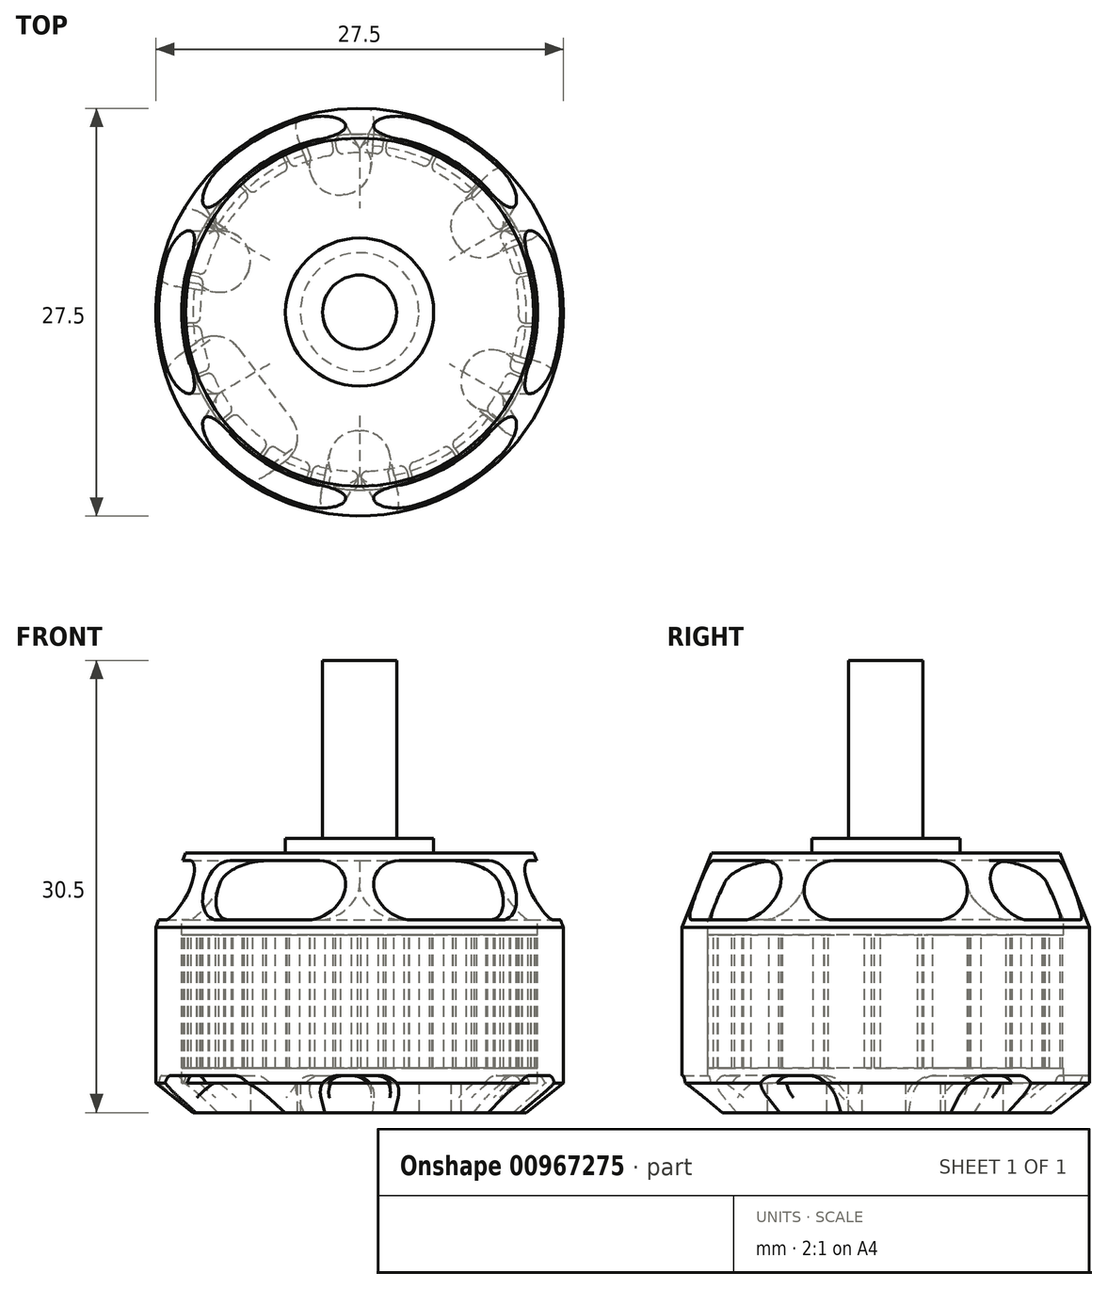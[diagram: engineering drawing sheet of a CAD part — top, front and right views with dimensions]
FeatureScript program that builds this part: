
annotation { "Feature Type Name" : "Feature", "Feature Type Description" : "" }
export const myFeature = defineFeature(function(context is Context, id is Id, definition is map)
    precondition{}
    {
        {
            var Q0;
            Q0=qCreatedBy(makeId("Top.planeOp"),FACE);
            var sketch = newSketch(context, id + "F0", { "sketchPlane" : qUnion([Q0])});
            skCircle(sketch, "E0", {"center": v(0, 0) * mm, "radius": 13.75 * mm});
            skSolve(sketch);
        }
        {
            var Q0;
            Q0=makeQuery(id+"F0.imprint","IMPRINT",FACE,{"disambiguationData":[TD([[makeQuery(id+"F0.imprint","IMPRINT",EDGE,{"derivedFrom":sQuery(id+"F0.wireOp",EDGE,"E0")}),1.0]])]});
            extrude(context, id + "F1", {"entities" : qUnion([Q0]), "depth" : 17.5 * mm});
        }
        {
            var Q0;
            Q0=makeQuery(id+"F1.opExtrude","CAP_FACE",FACE,{"disambiguationData":[OSD([sQuery(id+"F0.wireOp",EDGE,"E0")])],"isStart":false});
            var sketch = newSketch(context, id + "F2", { "sketchPlane" : qUnion([Q0])});
            skCircle(sketch, "E1", {"center": v(0, 0) * mm, "radius": 5 * mm});
            skSolve(sketch);
        }
        {
            var Q0;
            Q0=makeQuery(id+"F2.imprint","IMPRINT",FACE,{"disambiguationData":[TD([[makeQuery(id+"F2.imprint","IMPRINT",EDGE,{"derivedFrom":sQuery(id+"F2.wireOp",EDGE,"E1")}),1.0]])]});
            extrude(context, id + "F3", {"entities" : qUnion([Q0]), "operationType" : NewBodyOperationType.ADD, "depth" : 1 * mm});
        }
        {
            var Q0;
            Q0=makeQuery(id+"F3.opExtrude","CAP_FACE",FACE,{"disambiguationData":[OSD([sQuery(id+"F2.wireOp",EDGE,"E1")])],"isStart":false});
            var sketch = newSketch(context, id + "F4", { "sketchPlane" : qUnion([Q0])});
            skCircle(sketch, "E2", {"center": v(0, 0) * mm, "radius": 2.5 * mm});
            skSolve(sketch);
        }
        {
            var Q0;
            Q0=makeQuery(id+"F4.imprint","IMPRINT",FACE,{"disambiguationData":[TD([[makeQuery(id+"F4.imprint","IMPRINT",EDGE,{"derivedFrom":sQuery(id+"F4.wireOp",EDGE,"E2")}),1.0]])]});
            extrude(context, id + "F5", {"entities" : qUnion([Q0]), "operationType" : NewBodyOperationType.ADD, "depth" : 12 * mm});
        }
        {
            var Q0;
            Q0=makeQuery(id+"F1.opExtrude","CAP_EDGE",EDGE,{"disambiguationData":[OSD([sQuery(id+"F0.wireOp",EDGE,"E0")])],"isStart":false});
            chamfer(context, id + "F6", {"entities" : qUnion([Q0]), "chamferType" : ChamferType.TWO_OFFSETS, "width1" : 2 * mm, "oppositeDirection" : false, "width2" : 5 * mm, "tangentPropagation" : true});
        }
        {
            var Q0;
            Q0=makeQuery(id+"F1.opExtrude","CAP_EDGE",EDGE,{"disambiguationData":[OSD([sQuery(id+"F0.wireOp",EDGE,"E0")])],"isStart":true});
            chamfer(context, id + "F7", {"entities" : qUnion([Q0]), "chamferType" : ChamferType.TWO_OFFSETS, "width1" : 2 * mm, "oppositeDirection" : false, "width2" : 2.5 * mm, "tangentPropagation" : true});
        }
        {
            var Q0;
            Q0=qCreatedBy(makeId("Right.planeOp"),FACE);
            var sketch = newSketch(context, id + "F8", { "sketchPlane" : qUnion([Q0])});
            skLineSegment(sketch, "E3.bottom", {"start": v(-3.5, 17) * mm, "end": v(3.5, 17) * mm});
            skLineSegment(sketch, "E3.top", {"start": v(-3.5, 13) * mm, "end": v(3.5, 13) * mm});
            skLineSegment(sketch, "E3.left", {"start": v(-3.5, 17) * mm, "end": v(-3.5, 13) * mm, "construction": true});
            skLineSegment(sketch, "E3.right", {"start": v(3.5, 17) * mm, "end": v(3.5, 13) * mm, "construction": true});
            skArc(sketch, "E4", {"start": v(-3.5, 17) * mm, "mid": v(-5.5, 15) * mm, "end": v(-3.5, 13) * mm});
            skArc(sketch, "E5", {"start": v(3.5, 13) * mm, "mid": v(5.5, 15) * mm, "end": v(3.5, 17) * mm});
            skSolve(sketch);
        }
        {
            var Q0;
            Q0=qSketchRegion(id+"F8",true);
            extrude(context, id + "F9", {"entities" : qUnion([Q0]), "endBound" : BoundingType.SYMMETRIC, "oppositeDirection" : true, "depth" : 30 * mm});
        }
        {
            var Q0;
            Q0=makeQuery(id+"F9.opExtrude","SWEPT_BODY",BODY,{"disambiguationData":[OSD([sQuery(id+"F8.wireOp",EDGE,"E3.bottom"),sQuery(id+"F8.wireOp",EDGE,"E3.top"),sQuery(id+"F8.wireOp",EDGE,"E4"),sQuery(id+"F8.wireOp",EDGE,"E5")])]});
            var Q1;
            Q1=makeQuery(id+"F5.opExtrude","SWEPT_FACE",FACE,{"disambiguationData":[OSD([sQuery(id+"F4.wireOp",EDGE,"E2")])]});
            circularPattern(context, id + "F10", {"entities" : qUnion([Q0]), "axis" : qUnion([Q1]), "angle" : 180 * degree, "instanceCount" : 4, "equalSpace" : true});
        }
        {
            var Q0;
            Q0=makeQuery(id+"F10.opPattern","COPY",BODY,{"derivedFrom":makeQuery(id+"F9.opExtrude","SWEPT_BODY",BODY,{"disambiguationData":[OSD([sQuery(id+"F8.wireOp",EDGE,"E3.bottom"),sQuery(id+"F8.wireOp",EDGE,"E3.top"),sQuery(id+"F8.wireOp",EDGE,"E4"),sQuery(id+"F8.wireOp",EDGE,"E5")])]}),"instanceName":"1"});
            var Q1;
            Q1=makeQuery(id+"F10.opPattern","COPY",BODY,{"derivedFrom":makeQuery(id+"F9.opExtrude","SWEPT_BODY",BODY,{"disambiguationData":[OSD([sQuery(id+"F8.wireOp",EDGE,"E3.bottom"),sQuery(id+"F8.wireOp",EDGE,"E3.top"),sQuery(id+"F8.wireOp",EDGE,"E4"),sQuery(id+"F8.wireOp",EDGE,"E5")])]}),"instanceName":"2"});
            var Q2;
            Q2=makeQuery(id+"F9.opExtrude","SWEPT_BODY",BODY,{"disambiguationData":[OSD([sQuery(id+"F8.wireOp",EDGE,"E3.bottom"),sQuery(id+"F8.wireOp",EDGE,"E3.top"),sQuery(id+"F8.wireOp",EDGE,"E4"),sQuery(id+"F8.wireOp",EDGE,"E5")])]});
            var Q3;
            Q3=makeQuery(id+"F10.opPattern","COPY",BODY,{"derivedFrom":makeQuery(id+"F9.opExtrude","SWEPT_BODY",BODY,{"disambiguationData":[OSD([sQuery(id+"F8.wireOp",EDGE,"E3.bottom"),sQuery(id+"F8.wireOp",EDGE,"E3.top"),sQuery(id+"F8.wireOp",EDGE,"E4"),sQuery(id+"F8.wireOp",EDGE,"E5")])]}),"instanceName":"3"});
            booleanBodies(context, id + "F11", {"operationType" : BooleanOperationType.UNION, "tools" : qUnion([Q0, Q1, Q2, Q3])});
        }
        {
            var Q0;
            Q0=makeQuery(id+"F9.opExtrude","SWEPT_BODY",BODY,{"disambiguationData":[OSD([sQuery(id+"F8.wireOp",EDGE,"E3.bottom"),sQuery(id+"F8.wireOp",EDGE,"E3.top"),sQuery(id+"F8.wireOp",EDGE,"E4"),sQuery(id+"F8.wireOp",EDGE,"E5")])]});
            var Q1;
            Q1=makeQuery(id+"F10.opPattern","COPY",BODY,{"derivedFrom":makeQuery(id+"F9.opExtrude","SWEPT_BODY",BODY,{"disambiguationData":[OSD([sQuery(id+"F8.wireOp",EDGE,"E3.bottom"),sQuery(id+"F8.wireOp",EDGE,"E3.top"),sQuery(id+"F8.wireOp",EDGE,"E4"),sQuery(id+"F8.wireOp",EDGE,"E5")])]}),"instanceName":"1"});
            var Q2;
            Q2=makeQuery(id+"F10.opPattern","COPY",BODY,{"derivedFrom":makeQuery(id+"F9.opExtrude","SWEPT_BODY",BODY,{"disambiguationData":[OSD([sQuery(id+"F8.wireOp",EDGE,"E3.bottom"),sQuery(id+"F8.wireOp",EDGE,"E3.top"),sQuery(id+"F8.wireOp",EDGE,"E4"),sQuery(id+"F8.wireOp",EDGE,"E5")])]}),"instanceName":"2"});
            var Q3;
            Q3=makeQuery(id+"F1.opExtrude","SWEPT_BODY",BODY,{"disambiguationData":[OSD([sQuery(id+"F0.wireOp",EDGE,"E0")])]});
            booleanBodies(context, id + "F12", {"operationType" : BooleanOperationType.SUBTRACTION, "tools" : qUnion([Q0, Q1, Q2]), "targets" : qUnion([Q3])});
        }
        {
            var Q0;
            Q0=qCreatedBy(makeId("Right.planeOp"),FACE);
            var sketch = newSketch(context, id + "F13", { "sketchPlane" : qUnion([Q0])});
            skLineSegment(sketch, "E6", {"start": v(10.9, 15.44) * mm, "end": v(12, 13) * mm});
            skLineSegment(sketch, "E7", {"start": v(12, 13) * mm, "end": v(12, 2) * mm});
            skLineSegment(sketch, "E8", {"start": v(12, 2) * mm, "end": v(0, 2) * mm});
            skLineSegment(sketch, "E9", {"start": v(0, 2) * mm, "end": v(0, 15.44) * mm});
            skLineSegment(sketch, "E10", {"start": v(0, 15.44) * mm, "end": v(10.9, 15.44) * mm});
            skSolve(sketch);
        }
        {
            var Q0;
            Q0=qSketchRegion(id+"F13",true);
            var Q1;
            Q1=sQuery(id+"F13.wireOp",EDGE,"E9");
            revolve(context, id + "F14", {"operationType" : NewBodyOperationType.REMOVE, "entities" : qUnion([Q0]), "axis" : qUnion([Q1]), "revolveType" : RevolveType.FULL, "oppositeDirection" : true});
        }
        {
            var Q0;
            Q0=qCreatedBy(makeId("Top.planeOp"),FACE);
            cPlane(context, id + "F15", {"entities" : qUnion([Q0]), "cplaneType" : CPlaneType.OFFSET, "offset" : 12 * mm, "width" : 150 * mm, "height" : 150 * mm});
        }
        {
            var Q0;
            Q0=qCreatedBy(id+"F15.planeOp",FACE);
            var sketch = newSketch(context, id + "F16", { "sketchPlane" : qUnion([Q0])});
            skArc(sketch, "E11", {"start": v(1.26, 11.93) * mm, "mid": v(0, 12) * mm, "end": v(-1.26, 11.93) * mm});
            skArc(sketch, "E12", {"start": v(1.11, 10.7) * mm, "mid": v(0, 10.75) * mm, "end": v(-1.11, 10.7) * mm});
            skLineSegment(sketch, "E13", {"start": v(1.55, 11.03) * mm, "end": v(1.61, 11.48) * mm});
            skLineSegment(sketch, "E14", {"start": v(-1.55, 11.03) * mm, "end": v(-1.61, 11.48) * mm});
            skPoint(sketch, "E15.visualSharp", {"position": v(-1.5, 10.65) * mm});
            skArc(sketch, "E15.filletArc", {"start": v(-1.55, 11.03) * mm, "mid": v(-1.4, 10.77) * mm, "end": v(-1.11, 10.7) * mm});
            skPoint(sketch, "E16.visualSharp", {"position": v(1.5, 10.65) * mm});
            skArc(sketch, "E16.filletArc", {"start": v(1.11, 10.7) * mm, "mid": v(1.4, 10.77) * mm, "end": v(1.55, 11.03) * mm});
            skPoint(sketch, "E17.visualSharp", {"position": v(-1.67, 11.88) * mm});
            skArc(sketch, "E17.filletArc", {"start": v(-1.26, 11.93) * mm, "mid": v(-1.53, 11.78) * mm, "end": v(-1.61, 11.48) * mm});
            skPoint(sketch, "E18.visualSharp", {"position": v(1.67, 11.88) * mm});
            skArc(sketch, "E18.filletArc", {"start": v(1.61, 11.48) * mm, "mid": v(1.53, 11.78) * mm, "end": v(1.26, 11.93) * mm});
            skPoint(sketch, "E19.1.0", {"position": v(-1.7, 10.61) * mm});
            skPoint(sketch, "E19.1.1", {"position": v(-4.57, 9.73) * mm});
            skPoint(sketch, "E19.1.2", {"position": v(-1.9, 11.85) * mm});
            skPoint(sketch, "E19.1.3", {"position": v(-5.1, 10.86) * mm});
            skArc(sketch, "E19.1.4", {"start": v(-2.31, 11.77) * mm, "mid": v(-3.54, 11.47) * mm, "end": v(-4.72, 11.03) * mm});
            skArc(sketch, "E19.1.5", {"start": v(-2.09, 10.55) * mm, "mid": v(-3.17, 10.27) * mm, "end": v(-4.22, 9.89) * mm});
            skLineSegment(sketch, "E19.1.6", {"start": v(-1.77, 11) * mm, "end": v(-1.84, 11.45) * mm});
            skArc(sketch, "E19.1.7", {"start": v(-4.72, 11.03) * mm, "mid": v(-4.94, 10.8) * mm, "end": v(-4.93, 10.5) * mm});
            skArc(sketch, "E19.1.8", {"start": v(-4.73, 10.09) * mm, "mid": v(-4.51, 9.88) * mm, "end": v(-4.22, 9.89) * mm});
            skArc(sketch, "E19.1.9", {"start": v(-1.84, 11.45) * mm, "mid": v(-2, 11.71) * mm, "end": v(-2.31, 11.77) * mm});
            skLineSegment(sketch, "E19.1.10", {"start": v(-4.73, 10.09) * mm, "end": v(-4.93, 10.5) * mm});
            skArc(sketch, "E19.1.11", {"start": v(-2.09, 10.55) * mm, "mid": v(-1.84, 10.7) * mm, "end": v(-1.77, 11) * mm});
            skPoint(sketch, "E19.2.0", {"position": v(-4.76, 9.64) * mm});
            skPoint(sketch, "E19.2.1", {"position": v(-7.23, 7.95) * mm});
            skPoint(sketch, "E19.2.2", {"position": v(-5.31, 10.76) * mm});
            skPoint(sketch, "E19.2.3", {"position": v(-8.07, 8.88) * mm});
            skArc(sketch, "E19.2.4", {"start": v(-5.68, 10.57) * mm, "mid": v(-6.76, 9.91) * mm, "end": v(-7.76, 9.15) * mm});
            skArc(sketch, "E19.2.5", {"start": v(-5.1, 9.46) * mm, "mid": v(-6.06, 8.88) * mm, "end": v(-6.94, 8.2) * mm});
            skLineSegment(sketch, "E19.2.6", {"start": v(-4.93, 10) * mm, "end": v(-5.13, 10.4) * mm});
            skArc(sketch, "E19.2.7", {"start": v(-7.76, 9.15) * mm, "mid": v(-7.9, 8.87) * mm, "end": v(-7.8, 8.58) * mm});
            skArc(sketch, "E19.2.8", {"start": v(-7.5, 8.24) * mm, "mid": v(-7.23, 8.11) * mm, "end": v(-6.94, 8.2) * mm});
            skArc(sketch, "E19.2.9", {"start": v(-5.13, 10.4) * mm, "mid": v(-5.37, 10.6) * mm, "end": v(-5.68, 10.57) * mm});
            skLineSegment(sketch, "E19.2.10", {"start": v(-7.5, 8.24) * mm, "end": v(-7.8, 8.58) * mm});
            skArc(sketch, "E19.2.11", {"start": v(-5.1, 9.46) * mm, "mid": v(-4.91, 9.7) * mm, "end": v(-4.93, 10) * mm});
            skPoint(sketch, "E19.3.0", {"position": v(-7.4, 7.8) * mm});
            skPoint(sketch, "E19.3.1", {"position": v(-9.26, 5.47) * mm});
            skPoint(sketch, "E19.3.2", {"position": v(-8.25, 8.71) * mm});
            skPoint(sketch, "E19.3.3", {"position": v(-10.33, 6.1) * mm});
            skArc(sketch, "E19.3.4", {"start": v(-8.55, 8.43) * mm, "mid": v(-9.38, 7.48) * mm, "end": v(-10.12, 6.46) * mm});
            skArc(sketch, "E19.3.5", {"start": v(-7.67, 7.54) * mm, "mid": v(-8.4, 6.7) * mm, "end": v(-9.05, 5.8) * mm});
            skLineSegment(sketch, "E19.3.6", {"start": v(-7.66, 8.1) * mm, "end": v(-7.97, 8.42) * mm});
            skArc(sketch, "E19.3.7", {"start": v(-10.12, 6.46) * mm, "mid": v(-10.17, 6.15) * mm, "end": v(-9.98, 5.9) * mm});
            skArc(sketch, "E19.3.8", {"start": v(-9.6, 5.67) * mm, "mid": v(-9.3, 5.62) * mm, "end": v(-9.05, 5.8) * mm});
            skArc(sketch, "E19.3.9", {"start": v(-7.97, 8.42) * mm, "mid": v(-8.26, 8.54) * mm, "end": v(-8.55, 8.43) * mm});
            skLineSegment(sketch, "E19.3.10", {"start": v(-9.6, 5.67) * mm, "end": v(-9.98, 5.9) * mm});
            skArc(sketch, "E19.3.11", {"start": v(-7.67, 7.54) * mm, "mid": v(-7.55, 7.81) * mm, "end": v(-7.66, 8.1) * mm});
            skPoint(sketch, "E19.4.0", {"position": v(-9.36, 5.28) * mm});
            skPoint(sketch, "E19.4.1", {"position": v(-10.46, 2.5) * mm});
            skPoint(sketch, "E19.4.2", {"position": v(-10.45, 5.9) * mm});
            skPoint(sketch, "E19.4.3", {"position": v(-11.67, 2.79) * mm});
            skArc(sketch, "E19.4.4", {"start": v(-10.65, 5.53) * mm, "mid": v(-11.17, 4.38) * mm, "end": v(-11.57, 3.19) * mm});
            skArc(sketch, "E19.4.5", {"start": v(-9.55, 4.94) * mm, "mid": v(-10, 3.93) * mm, "end": v(-10.36, 2.87) * mm});
            skLineSegment(sketch, "E19.4.6", {"start": v(-9.7, 5.47) * mm, "end": v(-10.1, 5.7) * mm});
            skArc(sketch, "E19.4.7", {"start": v(-11.57, 3.19) * mm, "mid": v(-11.53, 2.88) * mm, "end": v(-11.28, 2.7) * mm});
            skArc(sketch, "E19.4.8", {"start": v(-10.84, 2.59) * mm, "mid": v(-10.54, 2.63) * mm, "end": v(-10.36, 2.87) * mm});
            skArc(sketch, "E19.4.9", {"start": v(-10.1, 5.7) * mm, "mid": v(-10.4, 5.73) * mm, "end": v(-10.65, 5.53) * mm});
            skLineSegment(sketch, "E19.4.10", {"start": v(-10.84, 2.59) * mm, "end": v(-11.28, 2.7) * mm});
            skArc(sketch, "E19.4.11", {"start": v(-9.55, 4.94) * mm, "mid": v(-9.52, 5.24) * mm, "end": v(-9.7, 5.47) * mm});
            skPoint(sketch, "E19.5.0", {"position": v(-10.5, 2.29) * mm});
            skPoint(sketch, "E19.5.1", {"position": v(-10.73, -0.7) * mm});
            skPoint(sketch, "E19.5.2", {"position": v(-11.73, 2.55) * mm});
            skPoint(sketch, "E19.5.3", {"position": v(-11.97, -0.78) * mm});
            skArc(sketch, "E19.5.4", {"start": v(-11.8, 2.15) * mm, "mid": v(-11.97, 0.9) * mm, "end": v(-12, -0.36) * mm});
            skArc(sketch, "E19.5.5", {"start": v(-10.58, 1.9) * mm, "mid": v(-10.72, 0.8) * mm, "end": v(-10.75, -0.31) * mm});
            skLineSegment(sketch, "E19.5.6", {"start": v(-10.89, 2.37) * mm, "end": v(-11.33, 2.47) * mm});
            skArc(sketch, "E19.5.7", {"start": v(-12, -0.36) * mm, "mid": v(-11.86, -0.65) * mm, "end": v(-11.57, -0.75) * mm});
            skArc(sketch, "E19.5.8", {"start": v(-11.12, -0.72) * mm, "mid": v(-10.85, -0.6) * mm, "end": v(-10.75, -0.31) * mm});
            skArc(sketch, "E19.5.9", {"start": v(-11.33, 2.47) * mm, "mid": v(-11.63, 2.4) * mm, "end": v(-11.8, 2.15) * mm});
            skLineSegment(sketch, "E19.5.10", {"start": v(-11.12, -0.72) * mm, "end": v(-11.57, -0.75) * mm});
            skArc(sketch, "E19.5.11", {"start": v(-10.58, 1.9) * mm, "mid": v(-10.64, 2.2) * mm, "end": v(-10.89, 2.37) * mm});
            skPoint(sketch, "E19.6.0", {"position": v(-10.71, -0.91) * mm});
            skPoint(sketch, "E19.6.1", {"position": v(-10.05, -3.83) * mm});
            skPoint(sketch, "E19.6.2", {"position": v(-11.96, -1.02) * mm});
            skPoint(sketch, "E19.6.3", {"position": v(-11.21, -4.27) * mm});
            skArc(sketch, "E19.6.4", {"start": v(-11.91, -1.43) * mm, "mid": v(-11.7, -2.67) * mm, "end": v(-11.35, -3.88) * mm});
            skArc(sketch, "E19.6.5", {"start": v(-10.67, -1.3) * mm, "mid": v(-10.48, -2.4) * mm, "end": v(-10.18, -3.46) * mm});
            skLineSegment(sketch, "E19.6.6", {"start": v(-11.1, -0.94) * mm, "end": v(-11.55, -0.98) * mm});
            skArc(sketch, "E19.6.7", {"start": v(-11.35, -3.88) * mm, "mid": v(-11.15, -4.12) * mm, "end": v(-10.83, -4.13) * mm});
            skArc(sketch, "E19.6.8", {"start": v(-10.41, -3.97) * mm, "mid": v(-10.2, -3.76) * mm, "end": v(-10.18, -3.46) * mm});
            skArc(sketch, "E19.6.9", {"start": v(-11.55, -0.98) * mm, "mid": v(-11.83, -1.13) * mm, "end": v(-11.91, -1.43) * mm});
            skLineSegment(sketch, "E19.6.10", {"start": v(-10.41, -3.97) * mm, "end": v(-10.83, -4.13) * mm});
            skArc(sketch, "E19.6.11", {"start": v(-10.67, -1.3) * mm, "mid": v(-10.82, -1.03) * mm, "end": v(-11.1, -0.94) * mm});
            skPoint(sketch, "E19.7.0", {"position": v(-9.97, -4.03) * mm});
            skPoint(sketch, "E19.7.1", {"position": v(-8.47, -6.62) * mm});
            skPoint(sketch, "E19.7.2", {"position": v(-11.13, -4.5) * mm});
            skPoint(sketch, "E19.7.3", {"position": v(-9.46, -7.39) * mm});
            skArc(sketch, "E19.7.4", {"start": v(-10.96, -4.88) * mm, "mid": v(-10.4, -6) * mm, "end": v(-9.7, -7.06) * mm});
            skArc(sketch, "E19.7.5", {"start": v(-9.82, -4.38) * mm, "mid": v(-9.3, -5.38) * mm, "end": v(-8.7, -6.31) * mm});
            skLineSegment(sketch, "E19.7.6", {"start": v(-10.33, -4.17) * mm, "end": v(-10.75, -4.34) * mm});
            skArc(sketch, "E19.7.7", {"start": v(-9.7, -7.06) * mm, "mid": v(-9.44, -7.22) * mm, "end": v(-9.14, -7.14) * mm});
            skArc(sketch, "E19.7.8", {"start": v(-8.78, -6.86) * mm, "mid": v(-8.63, -6.6) * mm, "end": v(-8.7, -6.31) * mm});
            skArc(sketch, "E19.7.9", {"start": v(-10.75, -4.34) * mm, "mid": v(-10.97, -4.56) * mm, "end": v(-10.96, -4.88) * mm});
            skLineSegment(sketch, "E19.7.10", {"start": v(-8.78, -6.86) * mm, "end": v(-9.14, -7.14) * mm});
            skArc(sketch, "E19.7.11", {"start": v(-9.82, -4.38) * mm, "mid": v(-10.03, -4.17) * mm, "end": v(-10.33, -4.17) * mm});
            skPoint(sketch, "E19.8.0", {"position": v(-8.34, -6.79) * mm});
            skPoint(sketch, "E19.8.1", {"position": v(-6.14, -8.82) * mm});
            skPoint(sketch, "E19.8.2", {"position": v(-9.3, -7.58) * mm});
            skPoint(sketch, "E19.8.3", {"position": v(-6.86, -9.85) * mm});
            skArc(sketch, "E19.8.4", {"start": v(-9.04, -7.9) * mm, "mid": v(-8.16, -8.8) * mm, "end": v(-7.2, -9.6) * mm});
            skArc(sketch, "E19.8.5", {"start": v(-8.09, -7.08) * mm, "mid": v(-7.31, -7.88) * mm, "end": v(-6.46, -8.6) * mm});
            skLineSegment(sketch, "E19.8.6", {"start": v(-8.64, -7.03) * mm, "end": v(-9, -7.32) * mm});
            skArc(sketch, "E19.8.7", {"start": v(-7.2, -9.6) * mm, "mid": v(-6.9, -9.68) * mm, "end": v(-6.63, -9.51) * mm});
            skArc(sketch, "E19.8.8", {"start": v(-6.37, -9.14) * mm, "mid": v(-6.3, -8.85) * mm, "end": v(-6.46, -8.6) * mm});
            skArc(sketch, "E19.8.9", {"start": v(-9, -7.32) * mm, "mid": v(-9.14, -7.6) * mm, "end": v(-9.04, -7.9) * mm});
            skLineSegment(sketch, "E19.8.10", {"start": v(-6.37, -9.14) * mm, "end": v(-6.63, -9.51) * mm});
            skArc(sketch, "E19.8.11", {"start": v(-8.09, -7.08) * mm, "mid": v(-8.36, -6.95) * mm, "end": v(-8.64, -7.03) * mm});
            skPoint(sketch, "E19.9.0", {"position": v(-5.97, -8.94) * mm});
            skPoint(sketch, "E19.9.1", {"position": v(-3.27, -10.24) * mm});
            skPoint(sketch, "E19.9.2", {"position": v(-6.66, -9.98) * mm});
            skPoint(sketch, "E19.9.3", {"position": v(-3.65, -11.43) * mm});
            skArc(sketch, "E19.9.4", {"start": v(-6.31, -10.2) * mm, "mid": v(-5.2, -10.81) * mm, "end": v(-4.04, -11.3) * mm});
            skArc(sketch, "E19.9.5", {"start": v(-5.64, -9.15) * mm, "mid": v(-4.66, -9.69) * mm, "end": v(-3.64, -10.12) * mm});
            skLineSegment(sketch, "E19.9.6", {"start": v(-6.18, -9.27) * mm, "end": v(-6.43, -9.64) * mm});
            skArc(sketch, "E19.9.7", {"start": v(-4.04, -11.3) * mm, "mid": v(-3.73, -11.28) * mm, "end": v(-3.53, -11.04) * mm});
            skArc(sketch, "E19.9.8", {"start": v(-3.4, -10.61) * mm, "mid": v(-3.41, -10.32) * mm, "end": v(-3.64, -10.12) * mm});
            skArc(sketch, "E19.9.9", {"start": v(-6.43, -9.64) * mm, "mid": v(-6.5, -9.95) * mm, "end": v(-6.31, -10.2) * mm});
            skLineSegment(sketch, "E19.9.10", {"start": v(-3.4, -10.61) * mm, "end": v(-3.53, -11.04) * mm});
            skArc(sketch, "E19.9.11", {"start": v(-5.64, -9.15) * mm, "mid": v(-5.94, -9.1) * mm, "end": v(-6.18, -9.27) * mm});
            skPoint(sketch, "E19.10.0", {"position": v(-3.07, -10.3) * mm});
            skPoint(sketch, "E19.10.1", {"position": v(-0.1, -10.75) * mm});
            skPoint(sketch, "E19.10.2", {"position": v(-3.42, -11.5) * mm});
            skPoint(sketch, "E19.10.3", {"position": v(-0.12, -12) * mm});
            skArc(sketch, "E19.10.4", {"start": v(-3.02, -11.61) * mm, "mid": v(-1.79, -11.87) * mm, "end": v(-0.53, -11.99) * mm});
            skArc(sketch, "E19.10.5", {"start": v(-2.7, -10.4) * mm, "mid": v(-1.6, -10.63) * mm, "end": v(-0.5, -10.74) * mm});
            skLineSegment(sketch, "E19.10.6", {"start": v(-3.18, -10.68) * mm, "end": v(-3.3, -11.11) * mm});
            skArc(sketch, "E19.10.7", {"start": v(-0.53, -11.99) * mm, "mid": v(-0.24, -11.88) * mm, "end": v(-0.12, -11.6) * mm});
            skArc(sketch, "E19.10.8", {"start": v(-0.11, -11.14) * mm, "mid": v(-0.22, -10.86) * mm, "end": v(-0.5, -10.74) * mm});
            skArc(sketch, "E19.10.9", {"start": v(-3.3, -11.11) * mm, "mid": v(-3.27, -11.42) * mm, "end": v(-3.02, -11.61) * mm});
            skLineSegment(sketch, "E19.10.10", {"start": v(-0.11, -11.14) * mm, "end": v(-0.12, -11.6) * mm});
            skArc(sketch, "E19.10.11", {"start": v(-2.7, -10.4) * mm, "mid": v(-3, -10.45) * mm, "end": v(-3.18, -10.68) * mm});
            skPoint(sketch, "E19.11.0", {"position": v(0.1, -10.75) * mm});
            skPoint(sketch, "E19.11.1", {"position": v(3.07, -10.3) * mm});
            skPoint(sketch, "E19.11.2", {"position": v(0.12, -12) * mm});
            skPoint(sketch, "E19.11.3", {"position": v(3.42, -11.5) * mm});
            skArc(sketch, "E19.11.4", {"start": v(0.53, -11.99) * mm, "mid": v(1.79, -11.87) * mm, "end": v(3.02, -11.61) * mm});
            skArc(sketch, "E19.11.5", {"start": v(0.5, -10.74) * mm, "mid": v(1.6, -10.63) * mm, "end": v(2.7, -10.4) * mm});
            skLineSegment(sketch, "E19.11.6", {"start": v(0.11, -11.14) * mm, "end": v(0.12, -11.6) * mm});
            skArc(sketch, "E19.11.7", {"start": v(3.02, -11.61) * mm, "mid": v(3.27, -11.42) * mm, "end": v(3.3, -11.11) * mm});
            skArc(sketch, "E19.11.8", {"start": v(3.18, -10.68) * mm, "mid": v(3, -10.45) * mm, "end": v(2.7, -10.4) * mm});
            skArc(sketch, "E19.11.9", {"start": v(0.12, -11.6) * mm, "mid": v(0.24, -11.88) * mm, "end": v(0.53, -11.99) * mm});
            skLineSegment(sketch, "E19.11.10", {"start": v(3.18, -10.68) * mm, "end": v(3.3, -11.11) * mm});
            skArc(sketch, "E19.11.11", {"start": v(0.5, -10.74) * mm, "mid": v(0.22, -10.86) * mm, "end": v(0.11, -11.14) * mm});
            skPoint(sketch, "E19.12.0", {"position": v(3.27, -10.24) * mm});
            skPoint(sketch, "E19.12.1", {"position": v(5.97, -8.94) * mm});
            skPoint(sketch, "E19.12.2", {"position": v(3.65, -11.43) * mm});
            skPoint(sketch, "E19.12.3", {"position": v(6.66, -9.98) * mm});
            skArc(sketch, "E19.12.4", {"start": v(4.04, -11.3) * mm, "mid": v(5.2, -10.81) * mm, "end": v(6.31, -10.2) * mm});
            skArc(sketch, "E19.12.5", {"start": v(3.64, -10.12) * mm, "mid": v(4.66, -9.69) * mm, "end": v(5.64, -9.15) * mm});
            skLineSegment(sketch, "E19.12.6", {"start": v(3.4, -10.61) * mm, "end": v(3.53, -11.04) * mm});
            skArc(sketch, "E19.12.7", {"start": v(6.31, -10.2) * mm, "mid": v(6.5, -9.95) * mm, "end": v(6.43, -9.64) * mm});
            skArc(sketch, "E19.12.8", {"start": v(6.18, -9.27) * mm, "mid": v(5.94, -9.1) * mm, "end": v(5.64, -9.15) * mm});
            skArc(sketch, "E19.12.9", {"start": v(3.53, -11.04) * mm, "mid": v(3.73, -11.28) * mm, "end": v(4.04, -11.3) * mm});
            skLineSegment(sketch, "E19.12.10", {"start": v(6.18, -9.27) * mm, "end": v(6.43, -9.64) * mm});
            skArc(sketch, "E19.12.11", {"start": v(3.64, -10.12) * mm, "mid": v(3.41, -10.32) * mm, "end": v(3.4, -10.61) * mm});
            skPoint(sketch, "E19.13.0", {"position": v(6.14, -8.82) * mm});
            skPoint(sketch, "E19.13.1", {"position": v(8.34, -6.79) * mm});
            skPoint(sketch, "E19.13.2", {"position": v(6.86, -9.85) * mm});
            skPoint(sketch, "E19.13.3", {"position": v(9.3, -7.58) * mm});
            skArc(sketch, "E19.13.4", {"start": v(7.2, -9.6) * mm, "mid": v(8.16, -8.8) * mm, "end": v(9.04, -7.9) * mm});
            skArc(sketch, "E19.13.5", {"start": v(6.46, -8.6) * mm, "mid": v(7.31, -7.88) * mm, "end": v(8.09, -7.08) * mm});
            skLineSegment(sketch, "E19.13.6", {"start": v(6.37, -9.14) * mm, "end": v(6.63, -9.51) * mm});
            skArc(sketch, "E19.13.7", {"start": v(9.04, -7.9) * mm, "mid": v(9.14, -7.6) * mm, "end": v(9, -7.32) * mm});
            skArc(sketch, "E19.13.8", {"start": v(8.64, -7.03) * mm, "mid": v(8.36, -6.95) * mm, "end": v(8.09, -7.08) * mm});
            skArc(sketch, "E19.13.9", {"start": v(6.63, -9.51) * mm, "mid": v(6.9, -9.68) * mm, "end": v(7.2, -9.6) * mm});
            skLineSegment(sketch, "E19.13.10", {"start": v(8.64, -7.03) * mm, "end": v(9, -7.32) * mm});
            skArc(sketch, "E19.13.11", {"start": v(6.46, -8.6) * mm, "mid": v(6.3, -8.85) * mm, "end": v(6.37, -9.14) * mm});
            skPoint(sketch, "E19.14.0", {"position": v(8.47, -6.62) * mm});
            skPoint(sketch, "E19.14.1", {"position": v(9.97, -4.03) * mm});
            skPoint(sketch, "E19.14.2", {"position": v(9.46, -7.39) * mm});
            skPoint(sketch, "E19.14.3", {"position": v(11.13, -4.5) * mm});
            skArc(sketch, "E19.14.4", {"start": v(9.7, -7.06) * mm, "mid": v(10.4, -6) * mm, "end": v(10.96, -4.88) * mm});
            skArc(sketch, "E19.14.5", {"start": v(8.7, -6.31) * mm, "mid": v(9.3, -5.38) * mm, "end": v(9.82, -4.38) * mm});
            skLineSegment(sketch, "E19.14.6", {"start": v(8.78, -6.86) * mm, "end": v(9.14, -7.14) * mm});
            skArc(sketch, "E19.14.7", {"start": v(10.96, -4.88) * mm, "mid": v(10.97, -4.56) * mm, "end": v(10.75, -4.34) * mm});
            skArc(sketch, "E19.14.8", {"start": v(10.33, -4.17) * mm, "mid": v(10.03, -4.17) * mm, "end": v(9.82, -4.38) * mm});
            skArc(sketch, "E19.14.9", {"start": v(9.14, -7.14) * mm, "mid": v(9.44, -7.22) * mm, "end": v(9.7, -7.06) * mm});
            skLineSegment(sketch, "E19.14.10", {"start": v(10.33, -4.17) * mm, "end": v(10.75, -4.34) * mm});
            skArc(sketch, "E19.14.11", {"start": v(8.7, -6.31) * mm, "mid": v(8.63, -6.6) * mm, "end": v(8.78, -6.86) * mm});
            skPoint(sketch, "E19.15.0", {"position": v(10.05, -3.83) * mm});
            skPoint(sketch, "E19.15.1", {"position": v(10.71, -0.91) * mm});
            skPoint(sketch, "E19.15.2", {"position": v(11.21, -4.27) * mm});
            skPoint(sketch, "E19.15.3", {"position": v(11.96, -1.02) * mm});
            skArc(sketch, "E19.15.4", {"start": v(11.35, -3.88) * mm, "mid": v(11.7, -2.67) * mm, "end": v(11.91, -1.43) * mm});
            skArc(sketch, "E19.15.5", {"start": v(10.18, -3.46) * mm, "mid": v(10.48, -2.4) * mm, "end": v(10.67, -1.3) * mm});
            skLineSegment(sketch, "E19.15.6", {"start": v(10.41, -3.97) * mm, "end": v(10.83, -4.13) * mm});
            skArc(sketch, "E19.15.7", {"start": v(11.91, -1.43) * mm, "mid": v(11.83, -1.13) * mm, "end": v(11.55, -0.98) * mm});
            skArc(sketch, "E19.15.8", {"start": v(11.1, -0.94) * mm, "mid": v(10.82, -1.03) * mm, "end": v(10.67, -1.3) * mm});
            skArc(sketch, "E19.15.9", {"start": v(10.83, -4.13) * mm, "mid": v(11.15, -4.12) * mm, "end": v(11.35, -3.88) * mm});
            skLineSegment(sketch, "E19.15.10", {"start": v(11.1, -0.94) * mm, "end": v(11.55, -0.98) * mm});
            skArc(sketch, "E19.15.11", {"start": v(10.18, -3.46) * mm, "mid": v(10.2, -3.76) * mm, "end": v(10.41, -3.97) * mm});
            skPoint(sketch, "E19.16.0", {"position": v(10.73, -0.7) * mm});
            skPoint(sketch, "E19.16.1", {"position": v(10.5, 2.29) * mm});
            skPoint(sketch, "E19.16.2", {"position": v(11.97, -0.78) * mm});
            skPoint(sketch, "E19.16.3", {"position": v(11.73, 2.55) * mm});
            skArc(sketch, "E19.16.4", {"start": v(12, -0.36) * mm, "mid": v(11.97, 0.9) * mm, "end": v(11.8, 2.15) * mm});
            skArc(sketch, "E19.16.5", {"start": v(10.75, -0.31) * mm, "mid": v(10.72, 0.8) * mm, "end": v(10.58, 1.9) * mm});
            skLineSegment(sketch, "E19.16.6", {"start": v(11.12, -0.72) * mm, "end": v(11.57, -0.75) * mm});
            skArc(sketch, "E19.16.7", {"start": v(11.8, 2.15) * mm, "mid": v(11.63, 2.4) * mm, "end": v(11.33, 2.47) * mm});
            skArc(sketch, "E19.16.8", {"start": v(10.89, 2.37) * mm, "mid": v(10.64, 2.2) * mm, "end": v(10.58, 1.9) * mm});
            skArc(sketch, "E19.16.9", {"start": v(11.57, -0.75) * mm, "mid": v(11.86, -0.65) * mm, "end": v(12, -0.36) * mm});
            skLineSegment(sketch, "E19.16.10", {"start": v(10.89, 2.37) * mm, "end": v(11.33, 2.47) * mm});
            skArc(sketch, "E19.16.11", {"start": v(10.75, -0.31) * mm, "mid": v(10.85, -0.6) * mm, "end": v(11.12, -0.72) * mm});
            skPoint(sketch, "E19.17.0", {"position": v(10.46, 2.5) * mm});
            skPoint(sketch, "E19.17.1", {"position": v(9.36, 5.28) * mm});
            skPoint(sketch, "E19.17.2", {"position": v(11.67, 2.79) * mm});
            skPoint(sketch, "E19.17.3", {"position": v(10.45, 5.9) * mm});
            skArc(sketch, "E19.17.4", {"start": v(11.57, 3.19) * mm, "mid": v(11.17, 4.38) * mm, "end": v(10.65, 5.53) * mm});
            skArc(sketch, "E19.17.5", {"start": v(10.36, 2.87) * mm, "mid": v(10, 3.93) * mm, "end": v(9.55, 4.94) * mm});
            skLineSegment(sketch, "E19.17.6", {"start": v(10.84, 2.59) * mm, "end": v(11.28, 2.7) * mm});
            skArc(sketch, "E19.17.7", {"start": v(10.65, 5.53) * mm, "mid": v(10.4, 5.73) * mm, "end": v(10.1, 5.7) * mm});
            skArc(sketch, "E19.17.8", {"start": v(9.7, 5.47) * mm, "mid": v(9.52, 5.24) * mm, "end": v(9.55, 4.94) * mm});
            skArc(sketch, "E19.17.9", {"start": v(11.28, 2.7) * mm, "mid": v(11.53, 2.88) * mm, "end": v(11.57, 3.19) * mm});
            skLineSegment(sketch, "E19.17.10", {"start": v(9.7, 5.47) * mm, "end": v(10.1, 5.7) * mm});
            skArc(sketch, "E19.17.11", {"start": v(10.36, 2.87) * mm, "mid": v(10.54, 2.63) * mm, "end": v(10.84, 2.59) * mm});
            skPoint(sketch, "E19.18.0", {"position": v(9.26, 5.47) * mm});
            skPoint(sketch, "E19.18.1", {"position": v(7.4, 7.8) * mm});
            skPoint(sketch, "E19.18.2", {"position": v(10.33, 6.1) * mm});
            skPoint(sketch, "E19.18.3", {"position": v(8.25, 8.71) * mm});
            skArc(sketch, "E19.18.4", {"start": v(10.12, 6.46) * mm, "mid": v(9.38, 7.48) * mm, "end": v(8.55, 8.43) * mm});
            skArc(sketch, "E19.18.5", {"start": v(9.05, 5.8) * mm, "mid": v(8.4, 6.7) * mm, "end": v(7.67, 7.54) * mm});
            skLineSegment(sketch, "E19.18.6", {"start": v(9.6, 5.67) * mm, "end": v(9.98, 5.9) * mm});
            skArc(sketch, "E19.18.7", {"start": v(8.55, 8.43) * mm, "mid": v(8.26, 8.54) * mm, "end": v(7.97, 8.42) * mm});
            skArc(sketch, "E19.18.8", {"start": v(7.66, 8.1) * mm, "mid": v(7.55, 7.81) * mm, "end": v(7.67, 7.54) * mm});
            skArc(sketch, "E19.18.9", {"start": v(9.98, 5.9) * mm, "mid": v(10.17, 6.15) * mm, "end": v(10.12, 6.46) * mm});
            skLineSegment(sketch, "E19.18.10", {"start": v(7.66, 8.1) * mm, "end": v(7.97, 8.42) * mm});
            skArc(sketch, "E19.18.11", {"start": v(9.05, 5.8) * mm, "mid": v(9.3, 5.62) * mm, "end": v(9.6, 5.67) * mm});
            skPoint(sketch, "E19.19.0", {"position": v(7.23, 7.95) * mm});
            skPoint(sketch, "E19.19.1", {"position": v(4.76, 9.64) * mm});
            skPoint(sketch, "E19.19.2", {"position": v(8.07, 8.88) * mm});
            skPoint(sketch, "E19.19.3", {"position": v(5.31, 10.76) * mm});
            skArc(sketch, "E19.19.4", {"start": v(7.76, 9.15) * mm, "mid": v(6.76, 9.91) * mm, "end": v(5.68, 10.57) * mm});
            skArc(sketch, "E19.19.5", {"start": v(6.94, 8.2) * mm, "mid": v(6.06, 8.88) * mm, "end": v(5.1, 9.46) * mm});
            skLineSegment(sketch, "E19.19.6", {"start": v(7.5, 8.24) * mm, "end": v(7.8, 8.58) * mm});
            skArc(sketch, "E19.19.7", {"start": v(5.68, 10.57) * mm, "mid": v(5.37, 10.6) * mm, "end": v(5.13, 10.4) * mm});
            skArc(sketch, "E19.19.8", {"start": v(4.93, 10) * mm, "mid": v(4.91, 9.7) * mm, "end": v(5.1, 9.46) * mm});
            skArc(sketch, "E19.19.9", {"start": v(7.8, 8.58) * mm, "mid": v(7.9, 8.87) * mm, "end": v(7.76, 9.15) * mm});
            skLineSegment(sketch, "E19.19.10", {"start": v(4.93, 10) * mm, "end": v(5.13, 10.4) * mm});
            skArc(sketch, "E19.19.11", {"start": v(6.94, 8.2) * mm, "mid": v(7.23, 8.11) * mm, "end": v(7.5, 8.24) * mm});
            skPoint(sketch, "E19.20.0", {"position": v(4.57, 9.73) * mm});
            skPoint(sketch, "E19.20.1", {"position": v(1.7, 10.61) * mm});
            skPoint(sketch, "E19.20.2", {"position": v(5.1, 10.86) * mm});
            skPoint(sketch, "E19.20.3", {"position": v(1.9, 11.85) * mm});
            skArc(sketch, "E19.20.4", {"start": v(4.72, 11.03) * mm, "mid": v(3.54, 11.47) * mm, "end": v(2.31, 11.77) * mm});
            skArc(sketch, "E19.20.5", {"start": v(4.22, 9.89) * mm, "mid": v(3.17, 10.27) * mm, "end": v(2.09, 10.55) * mm});
            skLineSegment(sketch, "E19.20.6", {"start": v(4.73, 10.09) * mm, "end": v(4.93, 10.5) * mm});
            skArc(sketch, "E19.20.7", {"start": v(2.31, 11.77) * mm, "mid": v(2, 11.71) * mm, "end": v(1.84, 11.45) * mm});
            skArc(sketch, "E19.20.8", {"start": v(1.77, 11) * mm, "mid": v(1.84, 10.7) * mm, "end": v(2.09, 10.55) * mm});
            skArc(sketch, "E19.20.9", {"start": v(4.93, 10.5) * mm, "mid": v(4.94, 10.8) * mm, "end": v(4.72, 11.03) * mm});
            skLineSegment(sketch, "E19.20.10", {"start": v(1.77, 11) * mm, "end": v(1.84, 11.45) * mm});
            skArc(sketch, "E19.20.11", {"start": v(4.22, 9.89) * mm, "mid": v(4.51, 9.88) * mm, "end": v(4.73, 10.09) * mm});
            skSolve(sketch);
        }
        {
            var Q0;
            Q0=qSketchRegion(id+"F16",true);
            extrude(context, id + "F17", {"entities" : qUnion([Q0]), "operationType" : NewBodyOperationType.ADD, "oppositeDirection" : true, "depth" : 9 * mm});
        }
        {
            var Q0;
            Q0=makeQuery(id+"F1.opExtrude","CAP_FACE",FACE,{"disambiguationData":[OSD([sQuery(id+"F0.wireOp",EDGE,"E0")])],"isStart":true});
            var sketch = newSketch(context, id + "F18", { "sketchPlane" : qUnion([Q0])});
            skArc(sketch, "E20", {"start": v(2.86, 13.45) * mm, "mid": v(0, 13.75) * mm, "end": v(-2.86, 13.45) * mm});
            skLineSegment(sketch, "E21", {"start": v(-2.86, 13.45) * mm, "end": v(-2.04, 9.58) * mm});
            skLineSegment(sketch, "E22", {"start": v(2.86, 13.45) * mm, "end": v(2.04, 9.58) * mm});
            skArc(sketch, "E23", {"start": v(0.06, 8) * mm, "mid": v(0, 8) * mm, "end": v(-0.06, 8) * mm});
            skPoint(sketch, "E24.visualSharp", {"position": v(-1.66, 7.83) * mm});
            skArc(sketch, "E24.filletArc", {"start": v(-2.04, 9.58) * mm, "mid": v(-1.33, 8.44) * mm, "end": v(-0.06, 8) * mm});
            skPoint(sketch, "E25.visualSharp", {"position": v(1.66, 7.83) * mm});
            skArc(sketch, "E25.filletArc", {"start": v(0.06, 8) * mm, "mid": v(1.33, 8.44) * mm, "end": v(2.04, 9.58) * mm});
            skPoint(sketch, "E26.1.0", {"position": v(6.17, 5.09) * mm});
            skArc(sketch, "E26.1.1", {"start": v(7.13, 3.64) * mm, "mid": v(8.1, 2.71) * mm, "end": v(9.44, 2.62) * mm});
            skPoint(sketch, "E26.1.2", {"position": v(7.7, 2.14) * mm});
            skArc(sketch, "E26.1.3", {"start": v(7.56, 6.23) * mm, "mid": v(6.87, 5.08) * mm, "end": v(7.07, 3.75) * mm});
            skLineSegment(sketch, "E26.1.4", {"start": v(13.25, 3.67) * mm, "end": v(9.44, 2.62) * mm});
            skLineSegment(sketch, "E26.1.5", {"start": v(10.6, 8.75) * mm, "end": v(7.56, 6.23) * mm});
            skArc(sketch, "E26.1.6", {"start": v(13.25, 3.67) * mm, "mid": v(12.2, 6.35) * mm, "end": v(10.6, 8.75) * mm});
            skArc(sketch, "E26.1.7", {"start": v(7.13, 3.64) * mm, "mid": v(7.1, 3.7) * mm, "end": v(7.07, 3.75) * mm});
            skPoint(sketch, "E26.2.0", {"position": v(7.36, -3.13) * mm});
            skArc(sketch, "E26.2.1", {"start": v(6.52, -4.64) * mm, "mid": v(6.15, -5.93) * mm, "end": v(6.68, -7.17) * mm});
            skPoint(sketch, "E26.2.2", {"position": v(5.46, -5.85) * mm});
            skArc(sketch, "E26.2.3", {"start": v(9.02, -3.83) * mm, "mid": v(7.68, -3.75) * mm, "end": v(6.6, -4.54) * mm});
            skLineSegment(sketch, "E26.2.4", {"start": v(9.38, -10.06) * mm, "end": v(6.68, -7.17) * mm});
            skLineSegment(sketch, "E26.2.5", {"start": v(12.66, -5.37) * mm, "end": v(9.02, -3.83) * mm});
            skArc(sketch, "E26.2.6", {"start": v(9.38, -10.06) * mm, "mid": v(11.26, -7.89) * mm, "end": v(12.66, -5.37) * mm});
            skArc(sketch, "E26.2.7", {"start": v(6.52, -4.64) * mm, "mid": v(6.55, -4.59) * mm, "end": v(6.6, -4.54) * mm});
            skPoint(sketch, "E26.3.0", {"position": v(0.63, -7.98) * mm});
            skArc(sketch, "E26.3.1", {"start": v(-1.1, -7.92) * mm, "mid": v(-2.42, -8.2) * mm, "end": v(-3.27, -9.24) * mm});
            skPoint(sketch, "E26.3.2", {"position": v(-2.67, -7.54) * mm});
            skArc(sketch, "E26.3.3", {"start": v(0.77, -9.77) * mm, "mid": v(0.22, -8.54) * mm, "end": v(-0.98, -7.94) * mm});
            skLineSegment(sketch, "E26.3.4", {"start": v(-4.59, -12.96) * mm, "end": v(-3.27, -9.24) * mm});
            skLineSegment(sketch, "E26.3.5", {"start": v(1.08, -13.7) * mm, "end": v(0.77, -9.77) * mm});
            skArc(sketch, "E26.3.6", {"start": v(-4.59, -12.96) * mm, "mid": v(-1.8, -13.63) * mm, "end": v(1.08, -13.7) * mm});
            skArc(sketch, "E26.3.7", {"start": v(-1.1, -7.92) * mm, "mid": v(-1.04, -7.93) * mm, "end": v(-0.98, -7.94) * mm});
            skPoint(sketch, "E26.4.0", {"position": v(-6.78, -4.24) * mm});
            skArc(sketch, "E26.4.1", {"start": v(-7.54, -2.68) * mm, "mid": v(-8.39, -1.63) * mm, "end": v(-9.7, -1.36) * mm});
            skPoint(sketch, "E26.4.2", {"position": v(-7.92, -1.11) * mm});
            skArc(sketch, "E26.4.3", {"start": v(-8.3, -5.2) * mm, "mid": v(-7.48, -4.14) * mm, "end": v(-7.5, -2.8) * mm});
            skLineSegment(sketch, "E26.4.4", {"start": v(-13.62, -1.91) * mm, "end": v(-9.7, -1.36) * mm});
            skLineSegment(sketch, "E26.4.5", {"start": v(-11.66, -7.29) * mm, "end": v(-8.3, -5.2) * mm});
            skArc(sketch, "E26.4.6", {"start": v(-13.62, -1.91) * mm, "mid": v(-12.92, -4.7) * mm, "end": v(-11.66, -7.29) * mm});
            skArc(sketch, "E26.4.7", {"start": v(-7.54, -2.68) * mm, "mid": v(-7.52, -2.74) * mm, "end": v(-7.5, -2.8) * mm});
            skLineSegment(sketch, "E26.anchor1", {"start": v(0, 0) * mm, "end": v(-1.66, 7.83) * mm, "construction": true});
            skLineSegment(sketch, "E26.anchor2", {"start": v(0, 0) * mm, "end": v(-6.78, -4.24) * mm, "construction": true});
            skSolve(sketch);
        }
        {
            var Q0;
            Q0=qSketchRegion(id+"F18",true);
            extrude(context, id + "F19", {"entities" : qUnion([Q0]), "operationType" : NewBodyOperationType.REMOVE, "oppositeDirection" : true, "depth" : 2.5 * mm});
        }
        {
            var Q0;
            Q0=makeQuery(id+"F19.boolean.opBoolean","COPY",EDGE,{"derivedFrom":makeQuery(id+"F19.opExtrude","CAP_EDGE",EDGE,{"disambiguationData":[OSD([sQuery(id+"F18.wireOp",EDGE,"E26.1.5")])],"isStart":false})});
            var Q1;
            Q1=makeQuery(id+"F19.boolean.opBoolean","COPY",EDGE,{"derivedFrom":makeQuery(id+"F19.opExtrude","CAP_EDGE",EDGE,{"disambiguationData":[OSD([sQuery(id+"F18.wireOp",EDGE,"E26.1.4")])],"isStart":false})});
            var Q2;
            Q2=makeQuery(id+"F19.boolean.opBoolean","COPY",EDGE,{"derivedFrom":makeQuery(id+"F19.opExtrude","CAP_EDGE",EDGE,{"disambiguationData":[OSD([sQuery(id+"F18.wireOp",EDGE,"E22")])],"isStart":false})});
            var Q3;
            Q3=makeQuery(id+"F19.boolean.opBoolean","COPY",EDGE,{"derivedFrom":makeQuery(id+"F19.opExtrude","CAP_EDGE",EDGE,{"disambiguationData":[OSD([sQuery(id+"F18.wireOp",EDGE,"E21")])],"isStart":false})});
            var Q4;
            Q4=makeQuery(id+"F19.boolean.opBoolean","COPY",EDGE,{"derivedFrom":makeQuery(id+"F19.opExtrude","CAP_EDGE",EDGE,{"disambiguationData":[OSD([sQuery(id+"F18.wireOp",EDGE,"E26.2.5")])],"isStart":false})});
            var Q5;
            Q5=makeQuery(id+"F19.boolean.opBoolean","COPY",EDGE,{"derivedFrom":makeQuery(id+"F19.opExtrude","CAP_EDGE",EDGE,{"disambiguationData":[OSD([sQuery(id+"F18.wireOp",EDGE,"E26.2.4")])],"isStart":false})});
            var Q6;
            Q6=makeQuery(id+"F19.boolean.opBoolean","COPY",EDGE,{"derivedFrom":makeQuery(id+"F19.opExtrude","CAP_EDGE",EDGE,{"disambiguationData":[OSD([sQuery(id+"F18.wireOp",EDGE,"E26.3.5")])],"isStart":false})});
            var Q7;
            Q7=makeQuery(id+"F19.boolean.opBoolean","COPY",EDGE,{"derivedFrom":makeQuery(id+"F19.opExtrude","CAP_EDGE",EDGE,{"disambiguationData":[OSD([sQuery(id+"F18.wireOp",EDGE,"E26.3.4")])],"isStart":false})});
            var Q8;
            Q8=makeQuery(id+"F19.boolean.opBoolean","COPY",EDGE,{"derivedFrom":makeQuery(id+"F19.opExtrude","CAP_EDGE",EDGE,{"disambiguationData":[OSD([sQuery(id+"F18.wireOp",EDGE,"E26.4.5")])],"isStart":false})});
            var Q9;
            Q9=makeQuery(id+"F19.boolean.opBoolean","COPY",EDGE,{"derivedFrom":makeQuery(id+"F19.opExtrude","CAP_EDGE",EDGE,{"disambiguationData":[OSD([sQuery(id+"F18.wireOp",EDGE,"E26.4.4")])],"isStart":false})});
            fillet(context, id + "F20", {"entities" : qUnion([Q0, Q1, Q2, Q3, Q4, Q5, Q6, Q7, Q8, Q9]), "radius" : 1.5 * mm, "tangentPropagation" : true, "allowEdgeOverflow" : false});
        }
        {
            var Q0;
            Q0=makeQuery(id+"F1.opExtrude","CAP_FACE",FACE,{"disambiguationData":[OSD([sQuery(id+"F0.wireOp",EDGE,"E0")])],"isStart":true});
            var sketch = newSketch(context, id + "F21", { "sketchPlane" : qUnion([Q0])});
            skCircle(sketch, "E27", {"center": v(0, 0) * mm, "radius": 4 * mm});
            skSolve(sketch);
        }
        {
            var Q0;
            Q0=qSketchRegion(id+"F21",true);
            extrude(context, id + "F22", {"entities" : qUnion([Q0]), "operationType" : NewBodyOperationType.REMOVE, "oppositeDirection" : true, "depth" : 5 * mm});
        }
        {
            var Q0;
            Q0=qCreatedBy(makeId("Right.planeOp"),FACE);
            var sketch = newSketch(context, id + "F23", { "sketchPlane" : qUnion([Q0])});
            skLineSegment(sketch, "E28", {"start": v(0, 0) * mm, "end": v(0, 44) * mm, "construction": true});
            skSolve(sketch);
        }
        {
            var Q0;
            Q0=sQuery(id+"F23.wireOp",EDGE,"E28");
            cPlane(context, id + "F24", {"entities" : qUnion([Q0]), "cplaneType" : CPlaneType.LINE_ANGLE, "offset" : 25 * mm, "angle" : 37 * degree, "width" : 150 * mm, "height" : 150 * mm});
        }
        {
            var Q0;
            Q0=qCreatedBy(id+"F24.planeOp",FACE);
            var sketch = newSketch(context, id + "F25", { "sketchPlane" : qUnion([Q0])});
            skLineSegment(sketch, "E29.bottom", {"start": v(3.5, 2.5) * mm, "end": v(-3.5, 2.5) * mm});
            skLineSegment(sketch, "E29.top", {"start": v(5, 0) * mm, "end": v(-5, 0) * mm});
            skLineSegment(sketch, "E29.left", {"start": v(5, 1) * mm, "end": v(5, 0) * mm});
            skLineSegment(sketch, "E29.right", {"start": v(-5, 1) * mm, "end": v(-5, 0) * mm});
            skPoint(sketch, "E30.visualSharp", {"position": v(5, 2.5) * mm});
            skArc(sketch, "E30.filletArc", {"start": v(5, 1) * mm, "mid": v(4.56, 2.06) * mm, "end": v(3.5, 2.5) * mm});
            skPoint(sketch, "E31.visualSharp", {"position": v(-5, 2.5) * mm});
            skArc(sketch, "E31.filletArc", {"start": v(-3.5, 2.5) * mm, "mid": v(-4.56, 2.06) * mm, "end": v(-5, 1) * mm});
            skSolve(sketch);
        }
        {
            var Q0;
            Q0=qSketchRegion(id+"F25",true);
            extrude(context, id + "F26", {"entities" : qUnion([Q0]), "operationType" : NewBodyOperationType.REMOVE, "oppositeDirection" : true, "depth" : 25 * mm, "hasSecondDirection" : true, "secondDirectionOppositeDirection" : true, "secondDirectionDepth" : 8 * mm});
        }
        {
            var Q0;
            Q0=makeQuery(id+"F26.boolean.opBoolean","COPY",EDGE,{"derivedFrom":makeQuery(id+"F26.opExtrude","CAP_EDGE",EDGE,{"disambiguationData":[OSD([sQuery(id+"F25.wireOp",EDGE,"E29.left")])],"isStart":true})});
            var Q1;
            Q1=makeQuery(id+"F26.boolean.opBoolean","COPY",EDGE,{"derivedFrom":makeQuery(id+"F26.opExtrude","CAP_EDGE",EDGE,{"disambiguationData":[OSD([sQuery(id+"F25.wireOp",EDGE,"E29.right")])],"isStart":true})});
            fillet(context, id + "F27", {"entities" : qUnion([Q0, Q1]), "radius" : 2 * mm, "tangentPropagation" : true, "allowEdgeOverflow" : false});
        }
    });
